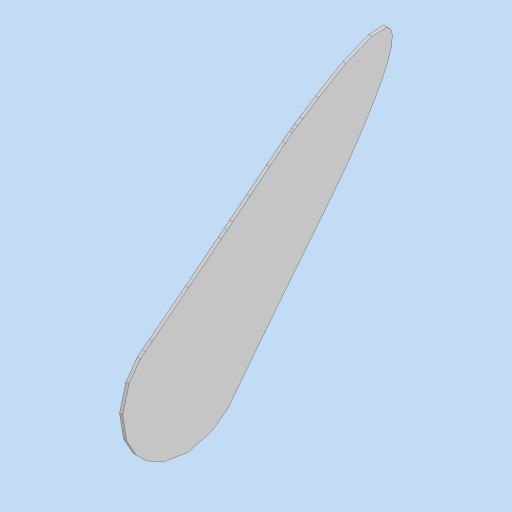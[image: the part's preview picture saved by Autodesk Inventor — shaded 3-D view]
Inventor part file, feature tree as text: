
AUTODESK INVENTOR PART (.ipt)
format: ipt  version: 2024 (Build 280153000, 153)  size: 238,592 bytes
history: native  units: mm
features: extrude x2, sketch x2
ambient origin geometry x8: Origin, YZ Plane, XZ Plane, XY Plane, X Axis, Y Axis, Z Axis, Center Point
bodies: Body1 (feature_tree)
feature tree (4):
  extrude  "Extrusion27"  Depth=0.25mm
  extrude  "Extrusion30"  Depth=10.0mm TaperAngle=0.0deg
  sketch  "Sketch1"  dims[d84=0.25mm d85=0.0mm d91=10.0mm]
  sketch  "Sketch7"  dims[d92=1.0mm d93=10.0mm d94=0.0mm d6=0.5mm d7=0.872665mm d8=0.5mm d9=0.872665mm]
